# Revit family: Соло
name_source: partatom
category: Оборудование
units: mm (PartAtom-declared; Revit-internal decimal feet)

## family parameters
Всегда вертикально = Да
Классификация = Нет
На основе рабочей плоскости = Нет
Общий = Нет
При загрузке вырезать с полостями = Нет
Размер круглого соединителя = Использовать диаметр
Тип детали = Нормальный
Точка принадлежности помещению = Нет

## types (3) — shared parameters
00_20_Виробник = Вентс
00_20_Назва = Реверсивний провітрювач
L = 305 мм
URL = https://vents.ua
l1 = 178 мм
Вага = 5.00 кг
Довжина = 401 мм
Изготовитель = Вентс
Класифікація навантаження = HVAC
Кількість фаз = 1
Матеріал зони обслуговуваня = <По категории>
Матеріал корпусу = Пластмаса, непрозора, біла
Напруга = 230 В
Струм = 0 А
Частота = 50 Гц
zero-valued in all types: Отметка по умолчанию

## per-type parameters (varying)
| type | B | B1 | D | Dy | L2 | b | l2 | Висота | Крышка задняя | Максимальний потік повітря | Потужність | Рівень звукового тиску на відстані 3 м | Ширина |
| Соло РA1-35-9 Р В.2 | 150 мм | 153 мм | 107 мм | 102 мм | 59 мм | 120 мм | 212 мм | 153 мм | Крышка задняя : 35 | 46.0 м³/ч | 2 Вт | 26 дБА | 153 мм |
| Соло РA1-50-9 Р В.2 | 175 мм | 186 мм | 131 мм | 126 мм | 86 мм | 145 мм | 239 мм | 186 мм | Крышка задняя : 50 | 50.0 м³/ч | 2 Вт | 29 дБА | 186 мм |
| Соло РA1-60-9 Р В.2 | 205 мм | 186 мм | 156 мм | 151 мм | 86 мм | 175 мм | 239 мм | 186 мм | Крышка задняя : 60 | 60.0 м³/ч | 3 Вт | 29 дБА | 186 мм |

note: column(s) folded — value = type name in every type: 00_20_Тип
